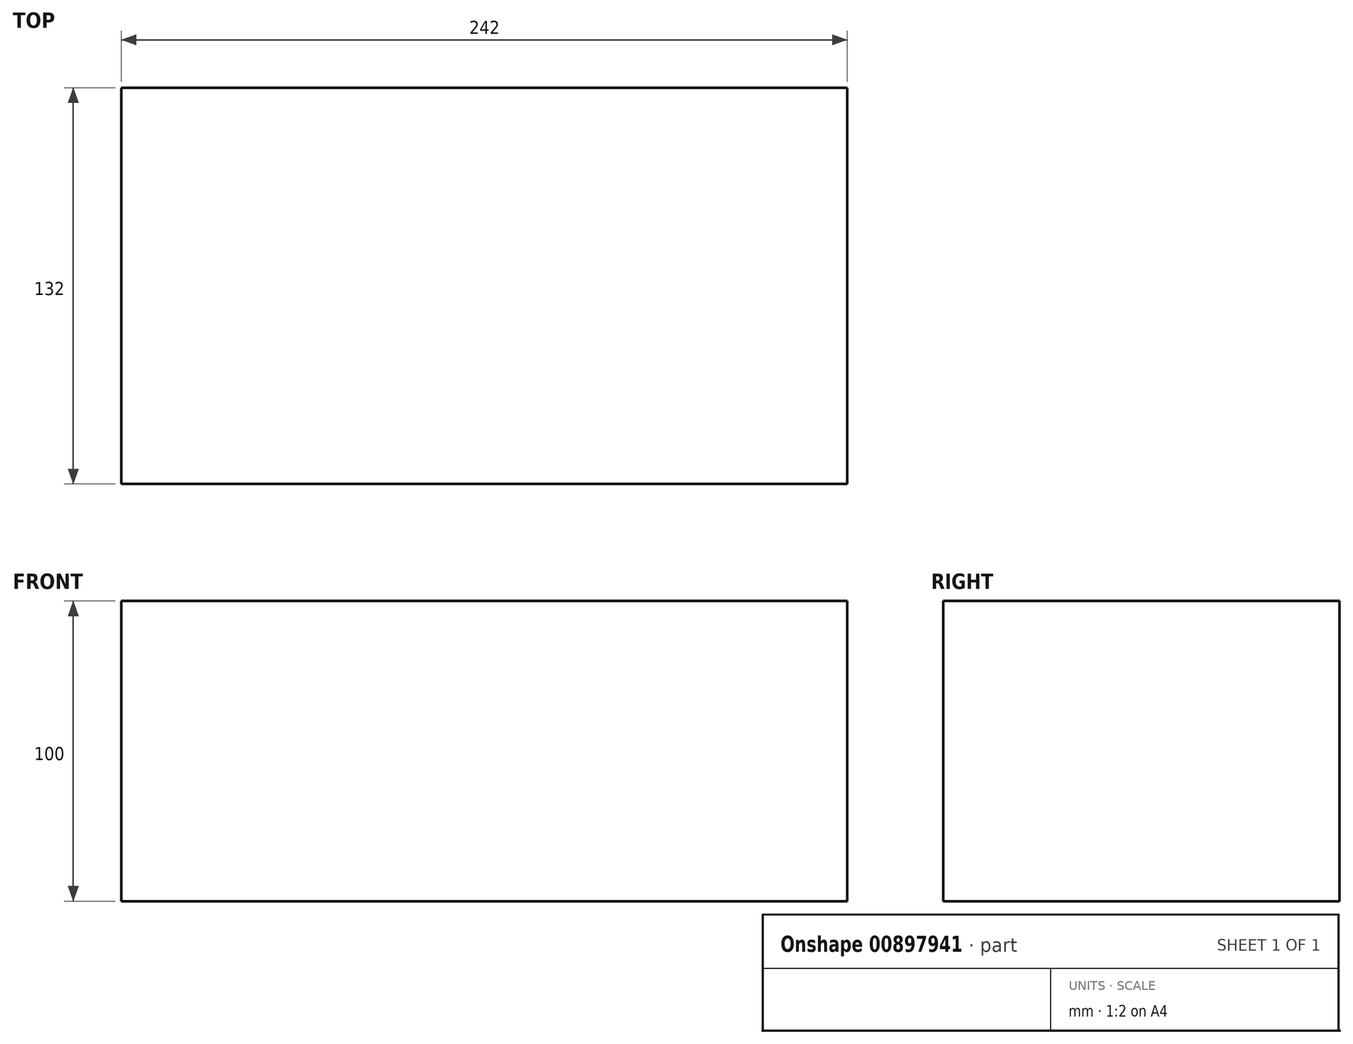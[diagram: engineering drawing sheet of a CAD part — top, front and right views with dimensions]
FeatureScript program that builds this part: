
annotation { "Feature Type Name" : "Feature", "Feature Type Description" : "" }
export const myFeature = defineFeature(function(context is Context, id is Id, definition is map)
    precondition{}
    {
        {
            var Q0;
            Q0=qCreatedBy(makeId("Top.planeOp"),FACE);
            var sketch = newSketch(context, id + "F0", { "sketchPlane" : qUnion([Q0])});
            skLineSegment(sketch, "E0.bottom", {"start": v(121, -66) * mm, "end": v(-121, -66) * mm});
            skLineSegment(sketch, "E0.top", {"start": v(121, 66) * mm, "end": v(-121, 66) * mm});
            skLineSegment(sketch, "E0.left", {"start": v(121, -66) * mm, "end": v(121, 66) * mm});
            skLineSegment(sketch, "E0.right", {"start": v(-121, -66) * mm, "end": v(-121, 66) * mm});
            skPoint(sketch, "E0.middle", {"position": v(0, 0) * mm});
            skSolve(sketch);
        }
        {
            var Q0;
            Q0 = qSketchRegion(id + "F0", true);
            var Q1;
            Q1 = qConstructionFilter(qBodyType(qCreatedBy(id + "F0" ,EDGE), BodyType.WIRE), ConstructionObject.NO);
            extrude(context, id + "F1", {"entities" : qUnion([Q0]), "surfaceEntities" : qUnion([Q1]), "depth" : 100 * mm, "offsetDistance" : 25 * mm});
        }
    });
